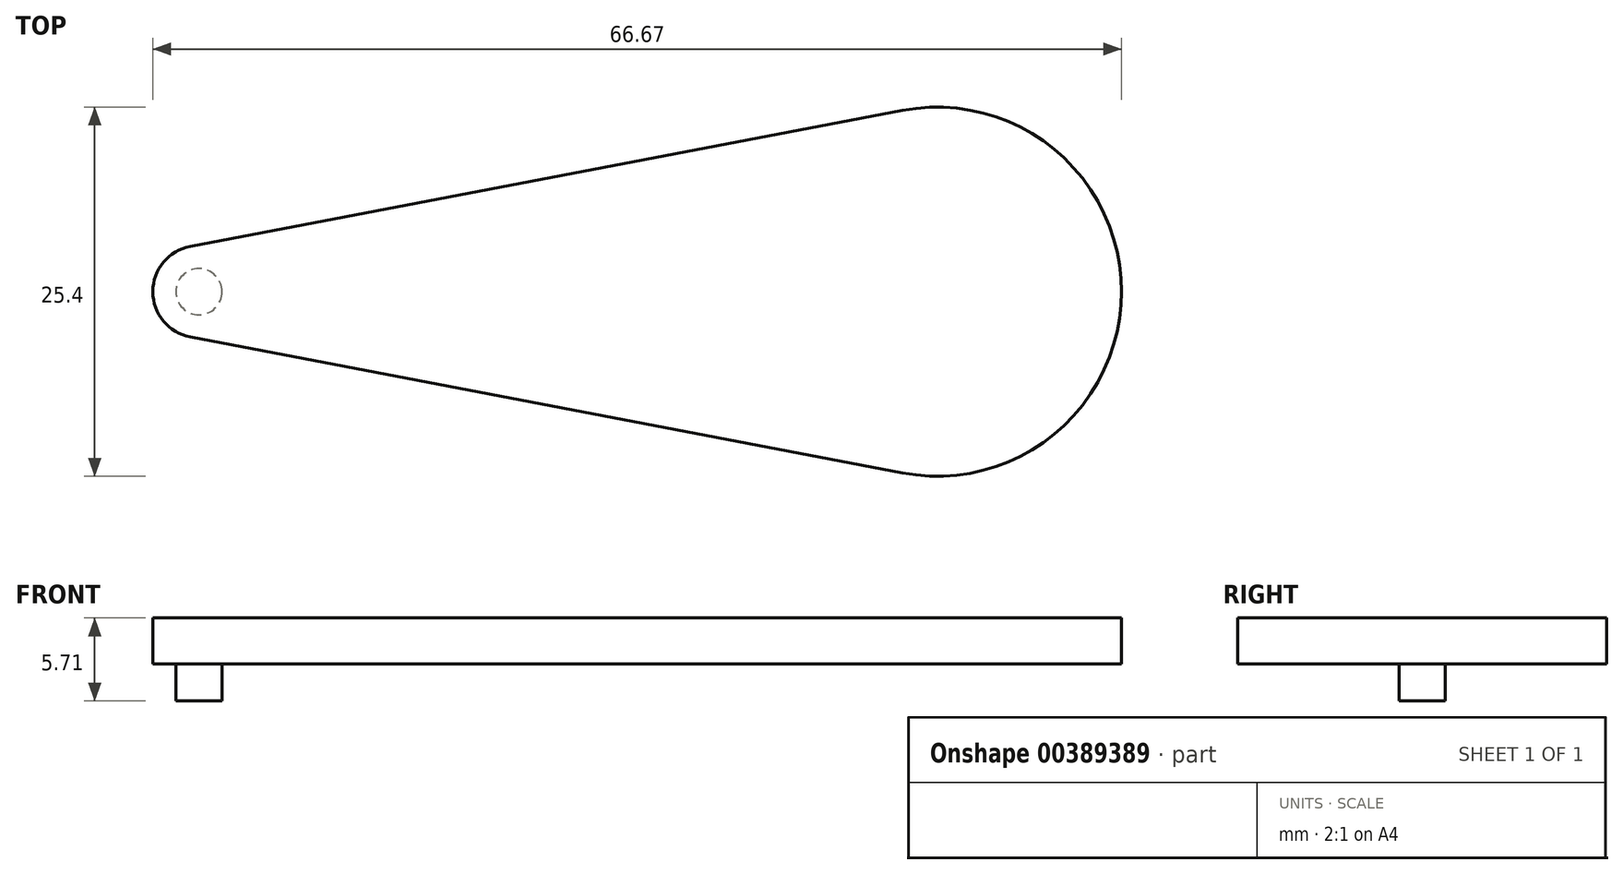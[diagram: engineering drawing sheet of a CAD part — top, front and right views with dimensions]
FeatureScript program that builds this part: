
annotation { "Feature Type Name" : "Feature", "Feature Type Description" : "" }
export const myFeature = defineFeature(function(context is Context, id is Id, definition is map)
    precondition{}
    {
        {
            var Q0;
            Q0=qCreatedBy(makeId("Top.planeOp"),FACE);
            var sketch = newSketch(context, id + "F0", { "sketchPlane" : qUnion([Q0])});
            skArc(sketch, "E0", {"start": v(-0.6, 3.12) * mm, "mid": v(-3.18, 0) * mm, "end": v(-0.6, -3.12) * mm});
            skCircle(sketch, "E1", {"center": v(0, 0) * mm, "radius": 1.59 * mm});
            skArc(sketch, "E2", {"start": v(48.42, -12.47) * mm, "mid": v(63.5, 0) * mm, "end": v(48.42, 12.47) * mm});
            skLineSegment(sketch, "E3", {"start": v(-0.6, 3.12) * mm, "end": v(48.42, 12.47) * mm});
            skLineSegment(sketch, "E4", {"start": v(-0.6, -3.12) * mm, "end": v(48.42, -12.47) * mm});
            skSolve(sketch);
        }
        {
            var Q0;
            Q0=makeQuery(id+"F0.imprint","IMPRINT",FACE,{"disambiguationData":[TD([[makeQuery(id+"F0.imprint","IMPRINT",EDGE,{"derivedFrom":sQuery(id+"F0.wireOp",EDGE,"E0")}),1.0]])]});
            var Q1;
            Q1=makeQuery(id+"F0.imprint","IMPRINT",FACE,{"disambiguationData":[TD([[makeQuery(id+"F0.imprint","IMPRINT",EDGE,{"derivedFrom":sQuery(id+"F0.wireOp",EDGE,"E1")}),1.0]])]});
            extrude(context, id + "F1", {"entities" : qUnion([Q0, Q1]), "depth" : 3.17 * mm});
        }
        {
            var Q0;
            Q0=makeQuery(id+"F0.imprint","IMPRINT",FACE,{"disambiguationData":[TD([[makeQuery(id+"F0.imprint","IMPRINT",EDGE,{"derivedFrom":sQuery(id+"F0.wireOp",EDGE,"E1")}),1.0]])]});
            extrude(context, id + "F2", {"entities" : qUnion([Q0]), "operationType" : NewBodyOperationType.ADD, "oppositeDirection" : true, "depth" : 2.54 * mm});
        }
    });
